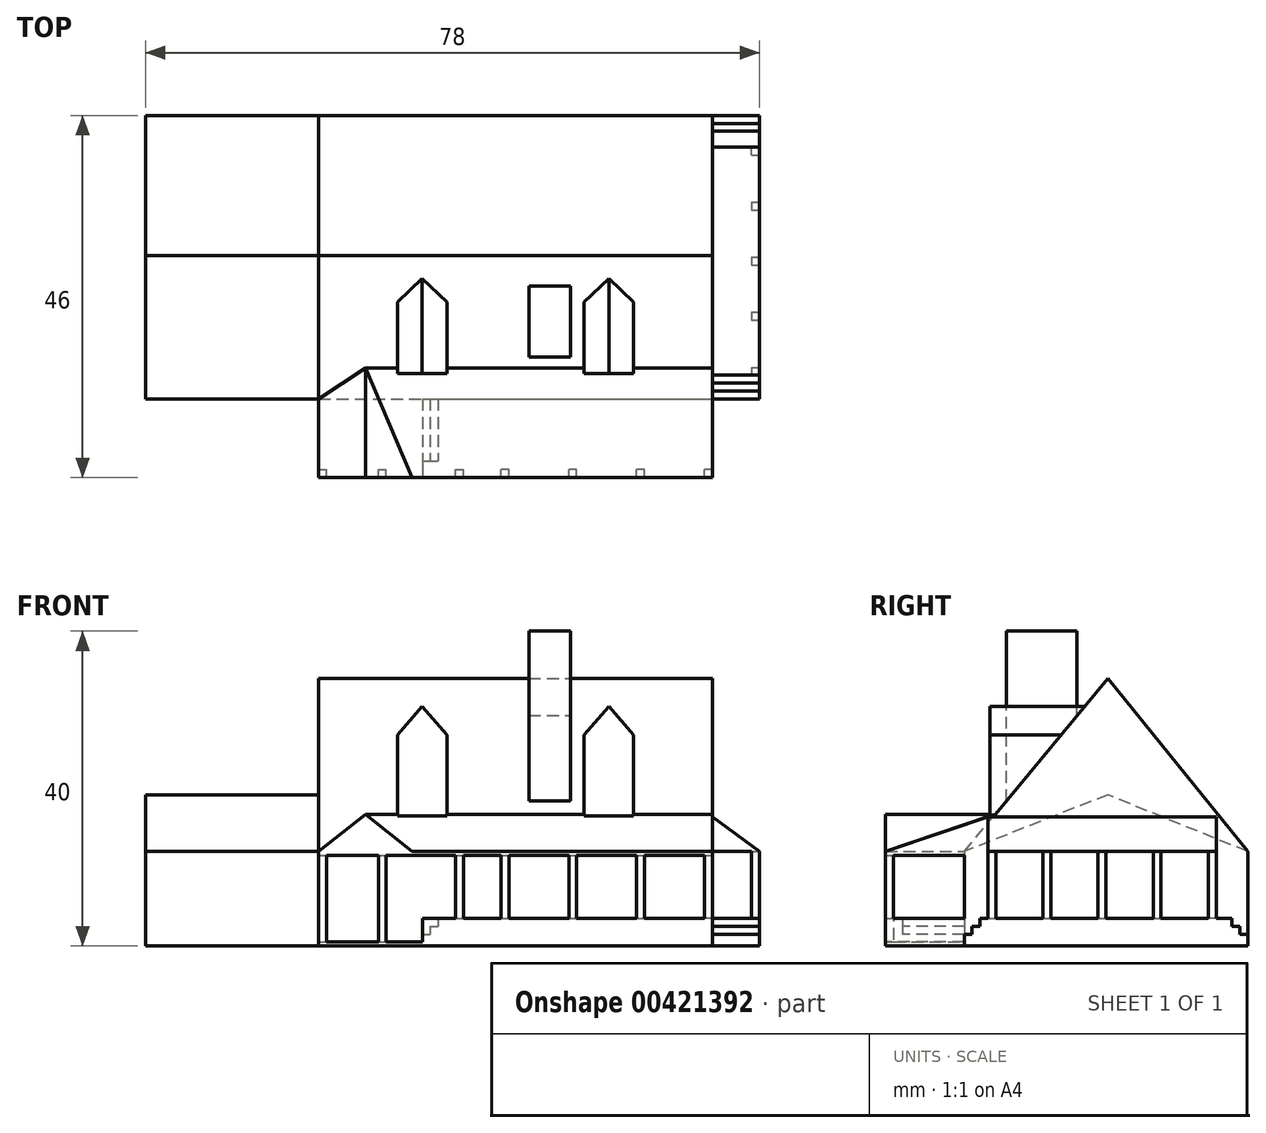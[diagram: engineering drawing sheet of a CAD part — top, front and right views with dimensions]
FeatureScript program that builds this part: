
annotation { "Feature Type Name" : "Feature", "Feature Type Description" : "" }
export const myFeature = defineFeature(function(context is Context, id is Id, definition is map)
    precondition{}
    {
        {
            var Q0;
            Q0=qCreatedBy(makeId("Top.planeOp"),FACE);
            var sketch = newSketch(context, id + "F0", { "sketchPlane" : qUnion([Q0])});
            skLineSegment(sketch, "E0.bottom", {"start": v(-54, 17.76) * mm, "end": v(18, 17.76) * mm});
            skLineSegment(sketch, "E0.top", {"start": v(-54, -18.24) * mm, "end": v(18, -18.24) * mm});
            skLineSegment(sketch, "E0.left", {"start": v(-54, 17.76) * mm, "end": v(-54, -18.24) * mm});
            skLineSegment(sketch, "E0.right", {"start": v(18, 17.76) * mm, "end": v(18, -18.24) * mm});
            skSolve(sketch);
        }
        {
            var Q0;
            Q0=makeQuery(id+"F0.imprint","IMPRINT",FACE,{"disambiguationData":[TD([[makeQuery(id+"F0.imprint","IMPRINT",EDGE,{"derivedFrom":sQuery(id+"F0.wireOp",EDGE,"E0.bottom")}),-1.0]])]});
            extrude(context, id + "F1", {"entities" : qUnion([Q0]), "depth" : 12 * mm});
        }
        {
            var Q0;
            Q0=makeQuery(id+"F1.opExtrude","SWEPT_FACE",FACE,{"disambiguationData":[OSD([sQuery(id+"F0.wireOp",EDGE,"E0.right")])]});
            var sketch = newSketch(context, id + "F2", { "sketchPlane" : qUnion([Q0])});
            skLineSegment(sketch, "E1.0", {"start": v(17.76, 12) * mm, "end": v(-18.24, 12) * mm});
            skLineSegment(sketch, "E2", {"start": v(-18.24, 12) * mm, "end": v(0, 33.97) * mm});
            skLineSegment(sketch, "E3", {"start": v(0, 33.97) * mm, "end": v(17.76, 12) * mm});
            skSolve(sketch);
        }
        {
            var Q0;
            Q0=makeQuery(id+"F2.imprint","IMPRINT",FACE,{"disambiguationData":[TD([[makeQuery(id+"F2.imprint","IMPRINT",EDGE,{"derivedFrom":sQuery(id+"F2.wireOp",EDGE,"E1.0")}),-1.0]])]});
            extrude(context, id + "F3", {"entities" : qUnion([Q0]), "operationType" : NewBodyOperationType.ADD, "oppositeDirection" : true, "depth" : 50 * mm});
        }
        {
            var Q0;
            Q0=makeQuery(id+"F1.opExtrude","SWEPT_FACE",FACE,{"disambiguationData":[OSD([sQuery(id+"F0.wireOp",EDGE,"E0.left")])]});
            var sketch = newSketch(context, id + "F4", { "sketchPlane" : qUnion([Q0])});
            skLineSegment(sketch, "E4.0", {"start": v(-17.76, 12) * mm, "end": v(18.24, 12) * mm});
            skLineSegment(sketch, "E5", {"start": v(-17.76, 12) * mm, "end": v(0, 19.2) * mm});
            skLineSegment(sketch, "E6", {"start": v(0, 19.2) * mm, "end": v(18.24, 12) * mm});
            skSolve(sketch);
        }
        {
            var Q0;
            Q0=makeQuery(id+"F4.imprint","IMPRINT",FACE,{"disambiguationData":[TD([[makeQuery(id+"F4.imprint","IMPRINT",EDGE,{"derivedFrom":sQuery(id+"F4.wireOp",EDGE,"E4.0")}),1.0]])]});
            extrude(context, id + "F5", {"entities" : qUnion([Q0]), "operationType" : NewBodyOperationType.ADD, "endBound" : BoundingType.UP_TO_NEXT, "oppositeDirection" : true, "depth" : 25 * mm});
        }
        {
            var Q0;
            Q0=makeQuery(id+"F1.opExtrude","SWEPT_FACE",FACE,{"disambiguationData":[OSD([sQuery(id+"F0.wireOp",EDGE,"E0.top")])]});
            var sketch = newSketch(context, id + "F6", { "sketchPlane" : qUnion([Q0])});
            skLineSegment(sketch, "E7.bottom", {"start": v(-32, 12) * mm, "end": v(18, 12) * mm});
            skLineSegment(sketch, "E7.top", {"start": v(-32, 11.5) * mm, "end": v(18, 11.5) * mm});
            skLineSegment(sketch, "E7.left", {"start": v(-32, 12) * mm, "end": v(-32, 11.5) * mm});
            skLineSegment(sketch, "E7.right", {"start": v(18, 12) * mm, "end": v(18, 11.5) * mm});
            skLineSegment(sketch, "E8", {"start": v(-32, 11.5) * mm, "end": v(-32, 0) * mm});
            skLineSegment(sketch, "E9.bottom", {"start": v(-32, 0) * mm, "end": v(18, 0) * mm});
            skLineSegment(sketch, "E9.top", {"start": v(-32, 0.5) * mm, "end": v(18, 0.5) * mm});
            skLineSegment(sketch, "E9.left", {"start": v(-32, 0) * mm, "end": v(-32, 0.5) * mm});
            skLineSegment(sketch, "E9.right", {"start": v(18, 0) * mm, "end": v(18, 0.5) * mm});
            skSolve(sketch);
        }
        {
            var Q0;
            Q0=makeQuery(id+"F6.imprint","IMPRINT",FACE,{"disambiguationData":[TD([[makeQuery(id+"F6.imprint","IMPRINT",EDGE,{"derivedFrom":sQuery(id+"F6.wireOp",EDGE,"E7.bottom")}),-1.0]])]});
            extrude(context, id + "F7", {"entities" : qUnion([Q0]), "operationType" : NewBodyOperationType.ADD, "depth" : 10 * mm});
        }
        {
            var Q0;
            Q0=makeQuery(id+"F6.imprint","IMPRINT",FACE,{"disambiguationData":[TD([[makeQuery(id+"F6.imprint","IMPRINT",EDGE,{"derivedFrom":sQuery(id+"F6.wireOp",EDGE,"E9.bottom")}),1.0]])]});
            extrude(context, id + "F8", {"entities" : qUnion([Q0]), "operationType" : NewBodyOperationType.ADD, "depth" : 10 * mm});
        }
        {
            var Q0;
            Q0=makeQuery(id+"F7.opExtrude","CAP_FACE",FACE,{"disambiguationData":[OSD([sQuery(id+"F6.wireOp",EDGE,"E7.bottom"),sQuery(id+"F6.wireOp",EDGE,"E7.top"),sQuery(id+"F6.wireOp",EDGE,"E7.left"),sQuery(id+"F6.wireOp",EDGE,"E7.right")])],"isStart":false});
            var sketch = newSketch(context, id + "F9", { "sketchPlane" : qUnion([Q0])});
            skLineSegment(sketch, "E10.0", {"start": v(-32, 12) * mm, "end": v(18, 12) * mm});
            skLineSegment(sketch, "E11", {"start": v(-32, 12) * mm, "end": v(-26.06, 16.73) * mm});
            skLineSegment(sketch, "E12", {"start": v(-26.06, 16.73) * mm, "end": v(-20.13, 12) * mm});
            skSolve(sketch);
        }
        {
            var Q0;
            {var subQ0=sQuery(id+"F9.wireOp",EDGE,"E11");Q0=makeQuery(id+"F9.imprint","IMPRINT",FACE,{"disambiguationData":[TD([[makeQuery(id+"F9.imprint","IMPRINT",EDGE,{"derivedFrom":subQ0}),-1.0]])]});}
            extrude(context, id + "F10", {"entities" : qUnion([Q0]), "operationType" : NewBodyOperationType.ADD, "endBound" : BoundingType.UP_TO_NEXT, "oppositeDirection" : true, "depth" : 25 * mm});
        }
        {
            var Q0;
            Q0=makeQuery(id+"F8.boolean.opBoolean","MERGE",FACE,{"derivedFrom":[makeQuery(id+"F7.boolean.opBoolean","MERGE",FACE,{"derivedFrom":[makeQuery(id+"F3.boolean.opBoolean","MERGE",FACE,{"derivedFrom":[makeQuery(id+"F1.opExtrude","SWEPT_FACE",FACE,{"disambiguationData":[OSD([sQuery(id+"F0.wireOp",EDGE,"E0.right")])]}),makeQuery(id+"F3.opExtrude","CAP_FACE",FACE,{"disambiguationData":[OSD([sQuery(id+"F2.wireOp",EDGE,"E1.0"),sQuery(id+"F2.wireOp",EDGE,"E2"),sQuery(id+"F2.wireOp",EDGE,"E3")])],"isStart":true})]}),makeQuery(id+"F7.opExtrude","SWEPT_FACE",FACE,{"disambiguationData":[OSD([sQuery(id+"F6.wireOp",EDGE,"E7.right")])]})]}),makeQuery(id+"F8.opExtrude","SWEPT_FACE",FACE,{"disambiguationData":[OSD([sQuery(id+"F6.wireOp",EDGE,"E9.right")])]})]});
            var sketch = newSketch(context, id + "F11", { "sketchPlane" : qUnion([Q0])});
            skLineSegment(sketch, "E13.0", {"start": v(-14.3, 16.73) * mm, "end": v(-28.24, 16.73) * mm});
            skLineSegment(sketch, "E14", {"start": v(-28.24, 12) * mm, "end": v(-14.3, 16.73) * mm});
            skSolve(sketch);
        }
        {
            var Q0;
            {var subQ0=sQuery(id+"F11.wireOp",EDGE,"E14");Q0=makeQuery(id+"F11.imprint","IMPRINT",FACE,{"disambiguationData":[TD([[makeQuery(id+"F11.imprint","IMPRINT",EDGE,{"derivedFrom":subQ0}),-1.0]])]});}
            extrude(context, id + "F12", {"entities" : qUnion([Q0]), "operationType" : NewBodyOperationType.ADD, "endBound" : BoundingType.UP_TO_NEXT, "oppositeDirection" : true, "depth" : 25 * mm});
        }
        {
            var Q0;
            Q0=makeQuery(id+"F8.opExtrude","SWEPT_FACE",FACE,{"disambiguationData":[OSD([sQuery(id+"F6.wireOp",EDGE,"E9.top")])]});
            var sketch = newSketch(context, id + "F13", { "sketchPlane" : qUnion([Q0])});
            skLineSegment(sketch, "E15", {"start": v(-18.82, -18.24) * mm, "end": v(-18.82, -28.24) * mm});
            skLineSegment(sketch, "E16", {"start": v(-17.82, -18.24) * mm, "end": v(-17.82, -28.24) * mm});
            skLineSegment(sketch, "E17", {"start": v(-16.82, -18.24) * mm, "end": v(-16.82, -28.24) * mm});
            skLineSegment(sketch, "E18.bottom", {"start": v(-32, -28.24) * mm, "end": v(-31, -28.24) * mm});
            skLineSegment(sketch, "E18.top", {"start": v(-32, -27.24) * mm, "end": v(-31, -27.24) * mm});
            skLineSegment(sketch, "E18.left", {"start": v(-32, -28.24) * mm, "end": v(-32, -27.24) * mm});
            skLineSegment(sketch, "E18.right", {"start": v(-31, -28.24) * mm, "end": v(-31, -27.24) * mm});
            skLineSegment(sketch, "E19.bottom", {"start": v(-24.4, -28.24) * mm, "end": v(-23.4, -28.24) * mm});
            skLineSegment(sketch, "E19.top", {"start": v(-24.4, -27.24) * mm, "end": v(-23.4, -27.24) * mm});
            skLineSegment(sketch, "E19.left", {"start": v(-24.4, -28.24) * mm, "end": v(-24.4, -27.24) * mm});
            skLineSegment(sketch, "E19.right", {"start": v(-23.4, -28.24) * mm, "end": v(-23.4, -27.24) * mm});
            skLineSegment(sketch, "E20", {"start": v(-31, -27.74) * mm, "end": v(-24.4, -27.74) * mm, "construction": true});
            skLineSegment(sketch, "E21", {"start": v(-23.4, -27.74) * mm, "end": v(-16.82, -27.51) * mm, "construction": true});
            skSolve(sketch);
        }
        {
            var Q0;
            {var subQ0=sQuery(id+"F13.wireOp",EDGE,"E15");Q0=makeQuery(id+"F13.imprint","IMPRINT",FACE,{"disambiguationData":[TD([[makeQuery(id+"F13.imprint","IMPRINT",EDGE,{"derivedFrom":subQ0}),1.0]])]});}
            extrude(context, id + "F14", {"entities" : qUnion([Q0]), "operationType" : NewBodyOperationType.ADD, "depth" : 1 * mm});
        }
        {
            var Q0;
            {var subQ0=sQuery(id+"F13.wireOp",EDGE,"E16");Q0=makeQuery(id+"F13.imprint","IMPRINT",FACE,{"disambiguationData":[TD([[makeQuery(id+"F13.imprint","IMPRINT",EDGE,{"derivedFrom":subQ0}),1.0]])]});}
            extrude(context, id + "F15", {"entities" : qUnion([Q0]), "operationType" : NewBodyOperationType.ADD, "depth" : 2 * mm});
        }
        {
            var Q0;
            {var subQ0=sQuery(id+"F13.wireOp",EDGE,"E17");Q0=makeQuery(id+"F13.imprint","IMPRINT",FACE,{"disambiguationData":[TD([[makeQuery(id+"F13.imprint","IMPRINT",EDGE,{"derivedFrom":subQ0}),1.0]])]});}
            extrude(context, id + "F16", {"entities" : qUnion([Q0]), "operationType" : NewBodyOperationType.ADD, "depth" : 3 * mm});
        }
        {
            var Q0;
            Q0=makeQuery(id+"F16.opExtrude","CAP_FACE",FACE,{"disambiguationData":[OSD([sQuery(id+"F0.wireOp",EDGE,"E0.top"),sQuery(id+"F0.wireOp",EDGE,"E0.right"),sQuery(id+"F6.wireOp",EDGE,"E9.top"),sQuery(id+"F6.wireOp",EDGE,"E9.right"),sQuery(id+"F13.wireOp",EDGE,"E17")])],"isStart":false});
            var sketch = newSketch(context, id + "F17", { "sketchPlane" : qUnion([Q0])});
            skLineSegment(sketch, "E22.bottom", {"start": v(18, -28.24) * mm, "end": v(17, -28.24) * mm});
            skLineSegment(sketch, "E22.top", {"start": v(18, -27.24) * mm, "end": v(17, -27.24) * mm});
            skLineSegment(sketch, "E22.left", {"start": v(18, -28.24) * mm, "end": v(18, -27.24) * mm});
            skLineSegment(sketch, "E22.right", {"start": v(17, -28.24) * mm, "end": v(17, -27.24) * mm});
            skLineSegment(sketch, "E23.bottom", {"start": v(9.4, -28.24) * mm, "end": v(8.4, -28.24) * mm});
            skLineSegment(sketch, "E23.top", {"start": v(9.4, -27.24) * mm, "end": v(8.4, -27.24) * mm});
            skLineSegment(sketch, "E23.left", {"start": v(9.4, -28.24) * mm, "end": v(9.4, -27.24) * mm});
            skLineSegment(sketch, "E23.right", {"start": v(8.4, -28.24) * mm, "end": v(8.4, -27.24) * mm});
            skLineSegment(sketch, "E24.bottom", {"start": v(0.79, -28.24) * mm, "end": v(-0.21, -28.24) * mm});
            skLineSegment(sketch, "E24.top", {"start": v(0.79, -27.24) * mm, "end": v(-0.21, -27.24) * mm});
            skLineSegment(sketch, "E24.left", {"start": v(0.79, -28.24) * mm, "end": v(0.79, -27.24) * mm});
            skLineSegment(sketch, "E24.right", {"start": v(-0.21, -28.24) * mm, "end": v(-0.21, -27.24) * mm});
            skLineSegment(sketch, "E25.bottom", {"start": v(-7.82, -28.24) * mm, "end": v(-8.82, -28.24) * mm});
            skLineSegment(sketch, "E25.top", {"start": v(-7.82, -27.24) * mm, "end": v(-8.82, -27.24) * mm});
            skLineSegment(sketch, "E25.left", {"start": v(-7.82, -28.24) * mm, "end": v(-7.82, -27.24) * mm});
            skLineSegment(sketch, "E25.right", {"start": v(-8.82, -28.24) * mm, "end": v(-8.82, -27.24) * mm});
            skLineSegment(sketch, "E26", {"start": v(-7.82, -27.74) * mm, "end": v(-0.21, -27.74) * mm, "construction": true});
            skLineSegment(sketch, "E27", {"start": v(0.79, -27.74) * mm, "end": v(8.4, -27.74) * mm, "construction": true});
            skLineSegment(sketch, "E28", {"start": v(9.4, -27.74) * mm, "end": v(17, -27.74) * mm, "construction": true});
            skLineSegment(sketch, "E29.bottom", {"start": v(-14.58, -28.24) * mm, "end": v(-13.58, -28.24) * mm});
            skLineSegment(sketch, "E29.top", {"start": v(-14.58, -27.24) * mm, "end": v(-13.58, -27.24) * mm});
            skLineSegment(sketch, "E29.left", {"start": v(-14.58, -28.24) * mm, "end": v(-14.58, -27.24) * mm});
            skLineSegment(sketch, "E29.right", {"start": v(-13.58, -28.24) * mm, "end": v(-13.58, -27.24) * mm});
            skSolve(sketch);
        }
        {
            var Q0;
            Q0=makeQuery(id+"F17.imprint","IMPRINT",FACE,{"disambiguationData":[TD([[makeQuery(id+"F17.imprint","IMPRINT",EDGE,{"derivedFrom":sQuery(id+"F17.wireOp",EDGE,"E29.bottom")}),1.0]])]});
            extrude(context, id + "F18", {"entities" : qUnion([Q0]), "operationType" : NewBodyOperationType.ADD, "endBound" : BoundingType.UP_TO_NEXT, "depth" : 25 * mm});
        }
        {
            var Q0;
            Q0=makeQuery(id+"F17.imprint","IMPRINT",FACE,{"disambiguationData":[TD([[makeQuery(id+"F17.imprint","IMPRINT",EDGE,{"derivedFrom":sQuery(id+"F17.wireOp",EDGE,"E25.bottom")}),1.0]])]});
            extrude(context, id + "F19", {"entities" : qUnion([Q0]), "operationType" : NewBodyOperationType.ADD, "endBound" : BoundingType.UP_TO_NEXT, "depth" : 25 * mm});
        }
        {
            var Q0;
            Q0=makeQuery(id+"F17.imprint","IMPRINT",FACE,{"disambiguationData":[TD([[makeQuery(id+"F17.imprint","IMPRINT",EDGE,{"derivedFrom":sQuery(id+"F17.wireOp",EDGE,"E24.bottom")}),1.0]])]});
            extrude(context, id + "F20", {"entities" : qUnion([Q0]), "operationType" : NewBodyOperationType.ADD, "endBound" : BoundingType.UP_TO_NEXT, "depth" : 25 * mm});
        }
        {
            var Q0;
            Q0=makeQuery(id+"F17.imprint","IMPRINT",FACE,{"disambiguationData":[TD([[makeQuery(id+"F17.imprint","IMPRINT",EDGE,{"derivedFrom":sQuery(id+"F17.wireOp",EDGE,"E23.bottom")}),1.0]])]});
            extrude(context, id + "F21", {"entities" : qUnion([Q0]), "operationType" : NewBodyOperationType.ADD, "endBound" : BoundingType.UP_TO_NEXT, "depth" : 25 * mm});
        }
        {
            var Q0;
            Q0=makeQuery(id+"F17.imprint","IMPRINT",FACE,{"disambiguationData":[TD([[makeQuery(id+"F17.imprint","IMPRINT",EDGE,{"derivedFrom":sQuery(id+"F17.wireOp",EDGE,"E22.bottom")}),1.0]])]});
            extrude(context, id + "F22", {"entities" : qUnion([Q0]), "operationType" : NewBodyOperationType.ADD, "endBound" : BoundingType.UP_TO_NEXT, "depth" : 25 * mm});
        }
        {
            var Q0;
            Q0=makeQuery(id+"F13.imprint","IMPRINT",FACE,{"disambiguationData":[TD([[makeQuery(id+"F13.imprint","IMPRINT",EDGE,{"derivedFrom":sQuery(id+"F13.wireOp",EDGE,"E18.bottom")}),1.0]])]});
            extrude(context, id + "F23", {"entities" : qUnion([Q0]), "operationType" : NewBodyOperationType.ADD, "endBound" : BoundingType.UP_TO_NEXT, "depth" : 25 * mm});
        }
        {
            var Q0;
            Q0=makeQuery(id+"F13.imprint","IMPRINT",FACE,{"disambiguationData":[TD([[makeQuery(id+"F13.imprint","IMPRINT",EDGE,{"derivedFrom":sQuery(id+"F13.wireOp",EDGE,"E19.bottom")}),1.0]])]});
            extrude(context, id + "F24", {"entities" : qUnion([Q0]), "operationType" : NewBodyOperationType.ADD, "endBound" : BoundingType.UP_TO_NEXT, "depth" : 25 * mm});
        }
        {
            var Q0;
            Q0=makeQuery(id+"F14.opExtrude","CAP_FACE",FACE,{"disambiguationData":[OSD([sQuery(id+"F6.wireOp",EDGE,"E9.top"),sQuery(id+"F13.wireOp",EDGE,"E15"),sQuery(id+"F13.wireOp",EDGE,"E16")])],"isStart":false});
            var sketch = newSketch(context, id + "F25", { "sketchPlane" : qUnion([Q0])});
            skLineSegment(sketch, "E30", {"start": v(-18.82, -26.1) * mm, "end": v(-17.82, -26.1) * mm});
            skSolve(sketch);
        }
        {
            var Q0;
            Q0=makeQuery(id+"F15.opExtrude","CAP_FACE",FACE,{"disambiguationData":[OSD([sQuery(id+"F6.wireOp",EDGE,"E9.top"),sQuery(id+"F13.wireOp",EDGE,"E16"),sQuery(id+"F13.wireOp",EDGE,"E17")])],"isStart":false});
            var sketch = newSketch(context, id + "F26", { "sketchPlane" : qUnion([Q0])});
            skPoint(sketch, "E31.0", {"position": v(-17.82, -26.1) * mm});
            skLineSegment(sketch, "E32", {"start": v(-17.82, -26.1) * mm, "end": v(-16.82, -26.1) * mm});
            skSolve(sketch);
        }
        {
            var Q0;
            {var subQ0=sQuery(id+"F25.wireOp",EDGE,"E30");Q0=makeQuery(id+"F25.imprint","IMPRINT",FACE,{"disambiguationData":[TD([[makeQuery(id+"F25.imprint","IMPRINT",EDGE,{"derivedFrom":subQ0}),-1.0]])]});}
            extrude(context, id + "F27", {"entities" : qUnion([Q0]), "operationType" : NewBodyOperationType.ADD, "depth" : 2 * mm});
        }
        {
            var Q0;
            {var subQ0=sQuery(id+"F26.wireOp",EDGE,"E32");Q0=makeQuery(id+"F26.imprint","IMPRINT",FACE,{"disambiguationData":[TD([[makeQuery(id+"F26.imprint","IMPRINT",EDGE,{"derivedFrom":subQ0}),-1.0]])]});}
            extrude(context, id + "F28", {"entities" : qUnion([Q0]), "operationType" : NewBodyOperationType.ADD, "depth" : 1 * mm});
        }
        {
            var Q0;
            {var subQ0=sQuery(id+"F6.wireOp",EDGE,"E9.right");var subQ1=sQuery(id+"F0.wireOp",EDGE,"E0.right");var subQ2=sQuery(id+"F6.wireOp",EDGE,"E7.right");var subQ3=sQuery(id+"F2.wireOp",EDGE,"E2");Q0=makeQuery(id+"F22.boolean.opBoolean","MERGE",FACE,{"derivedFrom":[makeQuery(id+"F16.boolean.opBoolean","MERGE",FACE,{"derivedFrom":[makeQuery(id+"F12.boolean.opBoolean","MERGE",FACE,{"derivedFrom":[makeQuery(id+"F8.boolean.opBoolean","MERGE",FACE,{"derivedFrom":[makeQuery(id+"F7.boolean.opBoolean","MERGE",FACE,{"derivedFrom":[makeQuery(id+"F3.boolean.opBoolean","MERGE",FACE,{"derivedFrom":[makeQuery(id+"F1.opExtrude","SWEPT_FACE",FACE,{"disambiguationData":[OSD([subQ1])]}),makeQuery(id+"F3.opExtrude","CAP_FACE",FACE,{"disambiguationData":[OSD([sQuery(id+"F2.wireOp",EDGE,"E1.0"),subQ3,sQuery(id+"F2.wireOp",EDGE,"E3")])],"isStart":true})]}),makeQuery(id+"F7.opExtrude","SWEPT_FACE",FACE,{"disambiguationData":[OSD([subQ2])]})]}),makeQuery(id+"F8.opExtrude","SWEPT_FACE",FACE,{"disambiguationData":[OSD([subQ0])]})]}),makeQuery(id+"F12.opExtrude","CAP_FACE",FACE,{"disambiguationData":[OSD([subQ3,sQuery(id+"F6.wireOp",EDGE,"E7.bottom"),subQ2,sQuery(id+"F11.wireOp",EDGE,"E14")])],"isStart":true})]}),makeQuery(id+"F16.opExtrude","SWEPT_FACE",FACE,{"disambiguationData":[OSD([sQuery(id+"F0.wireOp",EDGE,"E0.top"),subQ1,sQuery(id+"F6.wireOp",EDGE,"E9.top"),subQ0])]})]}),makeQuery(id+"F22.opExtrude","SWEPT_FACE",FACE,{"disambiguationData":[OSD([sQuery(id+"F17.wireOp",EDGE,"E22.left")])]})]});}
            var sketch = newSketch(context, id + "F29", { "sketchPlane" : qUnion([Q0])});
            skLineSegment(sketch, "E33.0", {"start": v(-18.24, 11.5) * mm, "end": v(-18.24, 3.5) * mm});
            skLineSegment(sketch, "E34", {"start": v(-18.24, 3.5) * mm, "end": v(-18.24, 0) * mm});
            skLineSegment(sketch, "E35", {"start": v(-18.24, 3.5) * mm, "end": v(17.76, 3.5) * mm});
            skSolve(sketch);
        }
        {
            var Q0;
            {var subQ0=sQuery(id+"F29.wireOp",EDGE,"E34");Q0=makeQuery(id+"F29.imprint","IMPRINT",FACE,{"disambiguationData":[TD([[makeQuery(id+"F29.imprint","IMPRINT",EDGE,{"derivedFrom":subQ0}),1.0]])]});}
            extrude(context, id + "F30", {"entities" : qUnion([Q0]), "operationType" : NewBodyOperationType.ADD, "depth" : 6 * mm});
        }
        {
            var Q0;
            Q0=makeQuery(id+"F30.opExtrude","SWEPT_FACE",FACE,{"disambiguationData":[OSD([sQuery(id+"F29.wireOp",EDGE,"E35")])]});
            var sketch = newSketch(context, id + "F31", { "sketchPlane" : qUnion([Q0])});
            skLineSegment(sketch, "E36", {"start": v(18, -17.24) * mm, "end": v(24, -17.24) * mm});
            skLineSegment(sketch, "E37", {"start": v(18, -16.24) * mm, "end": v(24, -16.24) * mm});
            skLineSegment(sketch, "E38", {"start": v(24, 16.76) * mm, "end": v(18, 16.76) * mm});
            skLineSegment(sketch, "E39", {"start": v(24, 15.76) * mm, "end": v(18, 15.76) * mm});
            skSolve(sketch);
        }
        {
            var Q0;
            {var subQ0=sQuery(id+"F31.wireOp",EDGE,"E36");Q0=makeQuery(id+"F31.imprint","IMPRINT",FACE,{"disambiguationData":[TD([[makeQuery(id+"F31.imprint","IMPRINT",EDGE,{"derivedFrom":subQ0}),-1.0]])]});}
            extrude(context, id + "F32", {"entities" : qUnion([Q0]), "operationType" : NewBodyOperationType.REMOVE, "oppositeDirection" : true, "depth" : 2 * mm});
        }
        {
            var Q0;
            {var subQ0=sQuery(id+"F31.wireOp",EDGE,"E36");Q0=makeQuery(id+"F31.imprint","IMPRINT",FACE,{"disambiguationData":[TD([[makeQuery(id+"F31.imprint","IMPRINT",EDGE,{"derivedFrom":subQ0}),1.0]])]});}
            extrude(context, id + "F33", {"entities" : qUnion([Q0]), "operationType" : NewBodyOperationType.REMOVE, "oppositeDirection" : true, "depth" : 1 * mm});
        }
        {
            var Q0;
            {var subQ0=sQuery(id+"F31.wireOp",EDGE,"E38");Q0=makeQuery(id+"F31.imprint","IMPRINT",FACE,{"disambiguationData":[TD([[makeQuery(id+"F31.imprint","IMPRINT",EDGE,{"derivedFrom":subQ0}),-1.0]])]});}
            extrude(context, id + "F34", {"entities" : qUnion([Q0]), "operationType" : NewBodyOperationType.REMOVE, "oppositeDirection" : true, "depth" : 2 * mm});
        }
        {
            var Q0;
            {var subQ0=sQuery(id+"F31.wireOp",EDGE,"E38");Q0=makeQuery(id+"F31.imprint","IMPRINT",FACE,{"disambiguationData":[TD([[makeQuery(id+"F31.imprint","IMPRINT",EDGE,{"derivedFrom":subQ0}),1.0]])]});}
            extrude(context, id + "F35", {"entities" : qUnion([Q0]), "operationType" : NewBodyOperationType.REMOVE, "oppositeDirection" : true, "depth" : 1 * mm});
        }
        {
            var Q0;
            {var subQ0=sQuery(id+"F0.wireOp",EDGE,"E0.bottom");Q0=makeQuery(id+"F30.boolean.opBoolean","MERGE",FACE,{"derivedFrom":[makeQuery(id+"F1.opExtrude","SWEPT_FACE",FACE,{"disambiguationData":[OSD([subQ0])]}),makeQuery(id+"F30.opExtrude","SWEPT_FACE",FACE,{"disambiguationData":[OSD([subQ0,sQuery(id+"F0.wireOp",EDGE,"E0.right")])]})]});}
            var sketch = newSketch(context, id + "F36", { "sketchPlane" : qUnion([Q0])});
            skLineSegment(sketch, "E40.0", {"start": v(-18, 33.97) * mm, "end": v(-18, 12) * mm});
            skPoint(sketch, "E41.0", {"position": v(-24, 3.5) * mm});
            skLineSegment(sketch, "E42", {"start": v(-24, 3.5) * mm, "end": v(-24, 12) * mm, "construction": true});
            skLineSegment(sketch, "E43", {"start": v(-24, 12) * mm, "end": v(-18, 12) * mm});
            skLineSegment(sketch, "E44", {"start": v(-24, 12) * mm, "end": v(-18, 16.4) * mm});
            skSolve(sketch);
        }
        {
            var Q0;
            {var subQ0=sQuery(id+"F36.wireOp",EDGE,"E43");Q0=makeQuery(id+"F36.imprint","IMPRINT",FACE,{"disambiguationData":[TD([[makeQuery(id+"F36.imprint","IMPRINT",EDGE,{"derivedFrom":subQ0}),1.0]])]});}
            extrude(context, id + "F37", {"entities" : qUnion([Q0]), "operationType" : NewBodyOperationType.ADD, "oppositeDirection" : true, "depth" : 33 * mm, "hasSecondDirection" : true, "secondDirectionOppositeDirection" : true, "secondDirectionDepth" : 4 * mm});
        }
        {
            var Q0;
            {var subQ0=sQuery(id+"F31.wireOp",EDGE,"E37");Q0=makeQuery(id+"F31.imprint","IMPRINT",FACE,{"disambiguationData":[TD([[makeQuery(id+"F31.imprint","IMPRINT",EDGE,{"derivedFrom":subQ0}),1.0]])]});}
            var sketch = newSketch(context, id + "F38", { "sketchPlane" : qUnion([Q0])});
            skPoint(sketch, "E45.0", {"position": v(24, -15.24) * mm});
            skPoint(sketch, "E46.0", {"position": v(24, 13.76) * mm});
            skLineSegment(sketch, "E47.bottom", {"start": v(24, -15.24) * mm, "end": v(23, -15.24) * mm});
            skLineSegment(sketch, "E47.top", {"start": v(24, -14.24) * mm, "end": v(23, -14.24) * mm});
            skLineSegment(sketch, "E47.left", {"start": v(24, -15.24) * mm, "end": v(24, -14.24) * mm});
            skLineSegment(sketch, "E47.right", {"start": v(23, -15.24) * mm, "end": v(23, -14.24) * mm});
            skLineSegment(sketch, "E48.0", {"start": v(24, -16.24) * mm, "end": v(24, 15.76) * mm});
            skLineSegment(sketch, "E49.bottom", {"start": v(24, -8.24) * mm, "end": v(23, -8.24) * mm});
            skLineSegment(sketch, "E49.top", {"start": v(24, -7.24) * mm, "end": v(23, -7.24) * mm});
            skLineSegment(sketch, "E49.left", {"start": v(24, -8.24) * mm, "end": v(24, -7.24) * mm});
            skLineSegment(sketch, "E49.right", {"start": v(23, -8.24) * mm, "end": v(23, -7.24) * mm});
            skLineSegment(sketch, "E50.bottom", {"start": v(24, -1.24) * mm, "end": v(23, -1.24) * mm});
            skLineSegment(sketch, "E50.top", {"start": v(24, -0.24) * mm, "end": v(23, -0.24) * mm});
            skLineSegment(sketch, "E50.left", {"start": v(24, -1.24) * mm, "end": v(24, -0.24) * mm});
            skLineSegment(sketch, "E50.right", {"start": v(23, -1.24) * mm, "end": v(23, -0.24) * mm});
            skLineSegment(sketch, "E51.bottom", {"start": v(24, 5.76) * mm, "end": v(23, 5.76) * mm});
            skLineSegment(sketch, "E51.top", {"start": v(24, 6.76) * mm, "end": v(23, 6.76) * mm});
            skLineSegment(sketch, "E51.left", {"start": v(24, 5.76) * mm, "end": v(24, 6.76) * mm});
            skLineSegment(sketch, "E51.right", {"start": v(23, 5.76) * mm, "end": v(23, 6.76) * mm});
            skLineSegment(sketch, "E52.bottom", {"start": v(24, 13.76) * mm, "end": v(23, 13.76) * mm});
            skLineSegment(sketch, "E52.top", {"start": v(24, 12.76) * mm, "end": v(23, 12.76) * mm});
            skLineSegment(sketch, "E52.left", {"start": v(24, 13.76) * mm, "end": v(24, 12.76) * mm});
            skLineSegment(sketch, "E52.right", {"start": v(23, 13.76) * mm, "end": v(23, 12.76) * mm});
            skLineSegment(sketch, "E53", {"start": v(23.5, 12.76) * mm, "end": v(23.5, 6.76) * mm, "construction": true});
            skLineSegment(sketch, "E54", {"start": v(23.5, 5.76) * mm, "end": v(23.5, -0.24) * mm, "construction": true});
            skLineSegment(sketch, "E55", {"start": v(23.5, -1.24) * mm, "end": v(23.5, -7.24) * mm, "construction": true});
            skLineSegment(sketch, "E56", {"start": v(23.5, -8.24) * mm, "end": v(23.5, -14.24) * mm, "construction": true});
            skSolve(sketch);
        }
        {
            var Q0;
            {var subQ0=sQuery(id+"F38.wireOp",EDGE,"E47.bottom");Q0=makeQuery(id+"F38.imprint","IMPRINT",FACE,{"disambiguationData":[TD([[makeQuery(id+"F38.imprint","IMPRINT",EDGE,{"derivedFrom":subQ0}),-1.0]])]});}
            extrude(context, id + "F39", {"entities" : qUnion([Q0]), "operationType" : NewBodyOperationType.ADD, "endBound" : BoundingType.UP_TO_NEXT, "depth" : 25 * mm});
        }
        {
            var Q0;
            Q0=makeQuery(id+"F38.imprint","IMPRINT",FACE,{"disambiguationData":[TD([[makeQuery(id+"F38.imprint","IMPRINT",EDGE,{"derivedFrom":sQuery(id+"F38.wireOp",EDGE,"E49.bottom")}),-1.0]])]});
            extrude(context, id + "F40", {"entities" : qUnion([Q0]), "operationType" : NewBodyOperationType.ADD, "endBound" : BoundingType.UP_TO_NEXT, "depth" : 25 * mm});
        }
        {
            var Q0;
            Q0=makeQuery(id+"F38.imprint","IMPRINT",FACE,{"disambiguationData":[TD([[makeQuery(id+"F38.imprint","IMPRINT",EDGE,{"derivedFrom":sQuery(id+"F38.wireOp",EDGE,"E50.bottom")}),-1.0]])]});
            extrude(context, id + "F41", {"entities" : qUnion([Q0]), "operationType" : NewBodyOperationType.ADD, "endBound" : BoundingType.UP_TO_NEXT, "depth" : 25 * mm});
        }
        {
            var Q0;
            Q0=makeQuery(id+"F38.imprint","IMPRINT",FACE,{"disambiguationData":[TD([[makeQuery(id+"F38.imprint","IMPRINT",EDGE,{"derivedFrom":sQuery(id+"F38.wireOp",EDGE,"E51.bottom")}),-1.0]])]});
            extrude(context, id + "F42", {"entities" : qUnion([Q0]), "operationType" : NewBodyOperationType.ADD, "endBound" : BoundingType.UP_TO_NEXT, "depth" : 25 * mm});
        }
        {
            var Q0;
            Q0=makeQuery(id+"F38.imprint","IMPRINT",FACE,{"disambiguationData":[TD([[makeQuery(id+"F38.imprint","IMPRINT",EDGE,{"derivedFrom":sQuery(id+"F38.wireOp",EDGE,"E52.bottom")}),1.0]])]});
            extrude(context, id + "F43", {"entities" : qUnion([Q0]), "operationType" : NewBodyOperationType.ADD, "endBound" : BoundingType.UP_TO_NEXT, "depth" : 25 * mm});
        }
        {
            var Q0;
            Q0=qCreatedBy(makeId("Front.planeOp"),FACE);
            cPlane(context, id + "F44", {"entities" : qUnion([Q0]), "cplaneType" : CPlaneType.OFFSET, "offset" : 15 * mm, "width" : 150 * mm, "height" : 150 * mm});
        }
        {
            var Q0;
            Q0=qCreatedBy(id+"F44.planeOp",FACE);
            var sketch = newSketch(context, id + "F45", { "sketchPlane" : qUnion([Q0])});
            skLineSegment(sketch, "E57.bottom", {"start": v(-22, 21.09) * mm, "end": v(-15.7, 21.09) * mm});
            skLineSegment(sketch, "E57.top", {"start": v(-22, 26.81) * mm, "end": v(-15.7, 26.81) * mm});
            skLineSegment(sketch, "E57.left", {"start": v(-22, 21.09) * mm, "end": v(-22, 26.81) * mm});
            skLineSegment(sketch, "E57.right", {"start": v(-15.7, 21.09) * mm, "end": v(-15.7, 26.81) * mm});
            skLineSegment(sketch, "E58", {"start": v(-22, 26.81) * mm, "end": v(-18.85, 30.4) * mm});
            skPoint(sketch, "E58.endSnap0", {"position": v(-18.85, 26.81) * mm});
            skLineSegment(sketch, "E59", {"start": v(-18.85, 30.4) * mm, "end": v(-15.7, 26.81) * mm});
            skLineSegment(sketch, "E60.0", {"start": v(-32, 12) * mm, "end": v(-32, 33.97) * mm});
            skLineSegment(sketch, "E61.0", {"start": v(18, 16.73) * mm, "end": v(18, 33.97) * mm});
            skLineSegment(sketch, "E62", {"start": v(-22, 23.95) * mm, "end": v(-32, 23.95) * mm, "construction": true});
            skLineSegment(sketch, "E63.bottom", {"start": v(1.73, 21.09) * mm, "end": v(8, 21.09) * mm});
            skLineSegment(sketch, "E63.top", {"start": v(1.73, 26.81) * mm, "end": v(8, 26.81) * mm});
            skLineSegment(sketch, "E63.left", {"start": v(1.73, 21.09) * mm, "end": v(1.73, 26.81) * mm});
            skLineSegment(sketch, "E63.right", {"start": v(8, 21.09) * mm, "end": v(8, 26.81) * mm});
            skLineSegment(sketch, "E64", {"start": v(1.73, 26.81) * mm, "end": v(4.87, 30.4) * mm});
            skPoint(sketch, "E64.endSnap0", {"position": v(4.87, 26.81) * mm});
            skLineSegment(sketch, "E65", {"start": v(4.87, 30.4) * mm, "end": v(8, 26.81) * mm});
            skLineSegment(sketch, "E66", {"start": v(8, 23.95) * mm, "end": v(18, 23.95) * mm, "construction": true});
            skSolve(sketch);
        }
        {
            var Q0;
            Q0=makeQuery(id+"F45.imprint","IMPRINT",FACE,{"disambiguationData":[TD([[makeQuery(id+"F45.imprint","IMPRINT",EDGE,{"derivedFrom":sQuery(id+"F45.wireOp",EDGE,"E57.bottom")}),1.0]])]});
            var Q1;
            Q1=makeQuery(id+"F45.imprint","IMPRINT",FACE,{"disambiguationData":[TD([[makeQuery(id+"F45.imprint","IMPRINT",EDGE,{"derivedFrom":sQuery(id+"F45.wireOp",EDGE,"E57.top")}),1.0]])]});
            extrude(context, id + "F46", {"entities" : qUnion([Q0, Q1]), "operationType" : NewBodyOperationType.ADD, "endBound" : BoundingType.UP_TO_NEXT, "oppositeDirection" : true, "depth" : 25 * mm});
        }
        {
            var Q0;
            Q0=makeQuery(id+"F45.imprint","IMPRINT",FACE,{"disambiguationData":[TD([[makeQuery(id+"F45.imprint","IMPRINT",EDGE,{"derivedFrom":sQuery(id+"F45.wireOp",EDGE,"E63.bottom")}),1.0]])]});
            var Q1;
            Q1=makeQuery(id+"F45.imprint","IMPRINT",FACE,{"disambiguationData":[TD([[makeQuery(id+"F45.imprint","IMPRINT",EDGE,{"derivedFrom":sQuery(id+"F45.wireOp",EDGE,"E63.top")}),1.0]])]});
            extrude(context, id + "F47", {"entities" : qUnion([Q0, Q1]), "operationType" : NewBodyOperationType.ADD, "endBound" : BoundingType.UP_TO_NEXT, "oppositeDirection" : true, "depth" : 25 * mm});
        }
        {
            var Q0;
            Q0=makeQuery(id+"F46.opExtrude","SWEPT_FACE",FACE,{"disambiguationData":[OSD([sQuery(id+"F45.wireOp",EDGE,"E57.bottom")])]});
            extrude(context, id + "F48", {"entities" : qUnion([Q0]), "operationType" : NewBodyOperationType.ADD, "endBound" : BoundingType.UP_TO_NEXT, "depth" : 25 * mm});
        }
        {
            var Q0;
            Q0=makeQuery(id+"F47.opExtrude","SWEPT_FACE",FACE,{"disambiguationData":[OSD([sQuery(id+"F45.wireOp",EDGE,"E63.bottom")])]});
            extrude(context, id + "F49", {"entities" : qUnion([Q0]), "operationType" : NewBodyOperationType.ADD, "endBound" : BoundingType.UP_TO_NEXT, "depth" : 25 * mm});
        }
        {
            var Q0;
            Q0=qCreatedBy(makeId("Top.planeOp"),FACE);
            cPlane(context, id + "F50", {"entities" : qUnion([Q0]), "cplaneType" : CPlaneType.OFFSET, "offset" : 40 * mm, "width" : 150 * mm, "height" : 150 * mm});
        }
        {
            var Q0;
            Q0=qCreatedBy(id+"F50.planeOp",FACE);
            var sketch = newSketch(context, id + "F51", { "sketchPlane" : qUnion([Q0])});
            skLineSegment(sketch, "E67.bottom", {"start": v(-5.3, -12.9) * mm, "end": v(0, -12.9) * mm});
            skLineSegment(sketch, "E67.top", {"start": v(-5.3, -3.9) * mm, "end": v(0, -3.9) * mm});
            skLineSegment(sketch, "E67.left", {"start": v(-5.3, -12.9) * mm, "end": v(-5.3, -3.9) * mm});
            skLineSegment(sketch, "E67.right", {"start": v(0, -12.9) * mm, "end": v(0, -3.9) * mm});
            skSolve(sketch);
        }
        {
            var Q0;
            Q0=makeQuery(id+"F51.imprint","IMPRINT",FACE,{"disambiguationData":[TD([[makeQuery(id+"F51.imprint","IMPRINT",EDGE,{"derivedFrom":sQuery(id+"F51.wireOp",EDGE,"E67.bottom")}),1.0]])]});
            extrude(context, id + "F52", {"entities" : qUnion([Q0]), "operationType" : NewBodyOperationType.ADD, "endBound" : BoundingType.UP_TO_NEXT, "oppositeDirection" : true, "depth" : 25 * mm});
        }
    });
